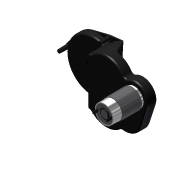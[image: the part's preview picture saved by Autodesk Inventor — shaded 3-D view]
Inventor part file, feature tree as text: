
AUTODESK INVENTOR PART (.ipt)
format: ipt  version: 2011 SP1 (Build 150282100, 282)  size: 314,880 bytes
history: native  units: mm (DEFAULTED — no unit token found)
features: sketch x13, extrude x12, fillet x7, plane x3, other x1, chamfer x1, pattern_circular x1
ambient origin geometry x8: Origin, YZ Plane, XZ Plane, XY Plane, X Axis, Y Axis, Z Axis, Center Point
bodies: Solid1 (feature_tree)
feature tree (38):
  extrude  "Extrusion1"  Depth=76.2mm
  fillet  "Fillet1"  Radius=43.18mm
  extrude  "Extrusion2"  Depth=53.848mm
  fillet  "Fillet2"  Radius=50.8mm
  fillet  "Fillet3"  Radius=3.048mm
  fillet  "Fillet4"  Radius=66.04mm
  fillet  "Fillet5"  Radius=34.29mm
  extrude  "Extrusion8"  Depth=41.91mm TaperAngle=0.0deg
  extrude  "Extrusion9"  Depth=28.448mm TaperAngle=0.0deg
  fillet  "Fillet9"  Radius=6.35mm
  extrude  "Extrusion10"  Depth=3.175mm
  other  "Work Axis1"
  sketch  "Sketch12"  dims[d19=3.175mm d22=15.24mm]
  plane  "Work Plane1"
  extrude  "Extrusion11"  Depth=15.24mm
  extrude  "Extrusion14"  Depth=78.3082mm
  extrude  "Extrusion15"  Depth=2.54mm TaperAngle=0.0deg
  plane  "Work Plane2"
  plane  "Work Plane3"
  extrude  "Extrusion16"  Depth=3.81mm
  fillet  "Fillet10"  Radius=7.62mm
  extrude  "Extrusion17"  Depth=25.4mm
  extrude  "Extrusion18"  Depth=25.4mm
  chamfer  "Chamfer1"  Distance=17.78mm
  pattern_circular  "Circular Pattern1"  [2 undecoded]
  sketch  "Sketch1"  dims[d0=99.06mm d1=76.2mm d2=43.18mm]
  sketch  "Sketch2"  dims[d3=53.848mm d4=53.848mm d5=50.8mm d7=3.048mm d8=66.04mm d9=34.29mm]
  sketch  "Sketch9"  dims[d10=19.05mm d11=41.91mm d12=0.0mm]
  sketch  "Sketch10"  dims[d13=6.35mm d14=28.448mm d15=0.0mm d16=6.35mm]
  sketch  "Sketch11"  dims[d17=3.175mm d18=3.175mm]
  sketch  "Sketch13"  dims[d43=8.89mm d44=78.3082mm]
  sketch  "Sketch15"  dims[d45=2.54mm d46=0.0mm d47=2.54mm d48=0.0mm]
  sketch  "Sketch16"  dims[d49=3.175mm d50=3.81mm d51=7.62mm]
  sketch  "Sketch17"  dims[d52=17.78mm d53=-0.349066mm d55=25.4mm]
  sketch  "Sketch18"  dims[d56=38.1mm d57=25.4mm d58=17.78mm d59=0.0mm]
  sketch  "Sketch19"  dims[d65=0.0mm d66=5.588mm]
  sketch  "Sketch20"  dims[d67=6.35mm d68=13.462mm d69=35.56mm d70=57.15mm d71=0.0mm d72=1.27mm d73=0.0mm d74=-16.002mm d75=-36.83mm d76=1.27mm d77=-1.047198mm d78=1.524mm d79=38.1mm d80=1.27mm d81=0.0mm d82=10.16mm d83=0.0mm d84=1.524mm d85=1.524mm d86=20.0mm d88=360.0deg d89=45.0deg]
  extrude  "Extrusion13"  Depth=57.15mm TaperAngle=0.0deg
note: 2 required parameter values undecoded (feature->parameter linkage not recoverable at this tier; creation-order binding heuristic only, values carry confidence <= 0.55)
